# Revit family: 304_F381_8__
name_source: partatom
category: Pipe Accessories
units: mm (PartAtom-declared; Revit-internal decimal feet)

## family parameters
Always vertical = Yes
Cut with Voids When Loaded = No
Part Type = Valve - Breaks Into
Round Connector Dimension = Use Diameter
Shared = No
Work Plane-Based = No

## types (3) — shared parameters
A = 60.00°
CenSd_RN_6 = 10 mm  [stored 0.0328084 ft]
Description = K - Automatic Balancing Valve - Accessible Pre-Set Cartridge
L2D_Min = 3048 mm  [stored 10 ft]
Manufacturer = FlowCon
QmdConnectorList = 301;D;302;D
R3 = 6 mm  [stored 0.019685 ft]
R4 = 11 mm  [stored 0.0360892 ft]
RN = 12 mm  [stored 0.0393701 ft]
URL = http://flowcon.com
magiPartTypeId = 304
magiProductFamilyId = F381.8.*
zero-valued in all types: MC_Default_elevation

## per-type parameters (varying)
| type | CenSd_SW_6 | D | H4 | H5 | H6 | L1 | L1__ve | L2 | L2D | L3 | L4 | LL | R | R1 | R2 | SW | W2D | magiProductId |
| F381.8.H.B | 16 mm  [stored 0.0524934 ft] | 25 mm | 49 mm | 73 mm | 43 mm | 24 mm  [stored 0.0787402 ft] | -24 mm  [stored -0.0787402 ft] | 102 mm  [stored 0.334646 ft] | 150 mm | 53 mm | 35 mm  [stored 0.114829 ft] | 75 mm  [stored 0.246063 ft] | 13 mm | 14 mm  [stored 0.0459318 ft] | 23 mm | 18 mm  [stored 0.0590551 ft] | 25 mm  [stored 0.082021 ft] | F381.8.H |
| F381.8.K.B | 22 mm | 40 mm | 51 mm  [stored 0.167323 ft] | 77 mm | 45 mm  [stored 0.147638 ft] | 25 mm  [stored 0.082021 ft] | -25 mm | 105 mm  [stored 0.344488 ft] | 155 mm | 54 mm | 36 mm | 78 mm | 20 mm  [stored 0.0656168 ft] | 20 mm  [stored 0.0656168 ft] | 28 mm  [stored 0.0918635 ft] | 25 mm  [stored 0.082021 ft] | 40 mm  [stored 0.131234 ft] | F381.8.K |
| F381.8.J.B | 17 mm | 32 mm | 51 mm  [stored 0.167323 ft] | 77 mm | 45 mm  [stored 0.147638 ft] | 25 mm  [stored 0.082021 ft] | -25 mm | 105 mm  [stored 0.344488 ft] | 155 mm | 54 mm | 36 mm | 78 mm | 16 mm  [stored 0.0524934 ft] | 16 mm  [stored 0.0524934 ft] | 26 mm | 20 mm  [stored 0.0656168 ft] | 32 mm  [stored 0.104987 ft] | F381.8.J |

note: column(s) folded — value = type name in every type: magiProductCode

note: [stored X ft] marks values corroborated as IEEE doubles in the binary element streams (Revit-internal decimal feet)

## geometry (parser evidence)
native form markers: Sweep x1
no freeform markers — native parametric forms only
